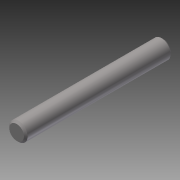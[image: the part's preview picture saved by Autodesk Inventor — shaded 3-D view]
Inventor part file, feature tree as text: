
AUTODESK INVENTOR PART (.ipt)
format: ipt  version: 2015 (Build 190159000, 159)  size: 102,912 bytes
history: native  units: in
note: dims shown in document units (in); Inventor stores cm internally (conversion verified against a paired STEP export)
features: revolve x1, other x1, imported_body x1
ambient origin geometry x8: Origin, YZ Plane, XZ Plane, XY Plane, X Axis, Y Axis, Z Axis, Center Point
bodies: Body1 (feature_tree)
feature tree (3):
  revolve  "Revolve1"  [1 undecoded]
  other  "tetrix_731132_roller_axle1"
  imported_body  "Base1"
note: 1 required parameter value undecoded (feature->parameter linkage not recoverable at this tier; creation-order binding heuristic only, values carry confidence <= 0.55)
